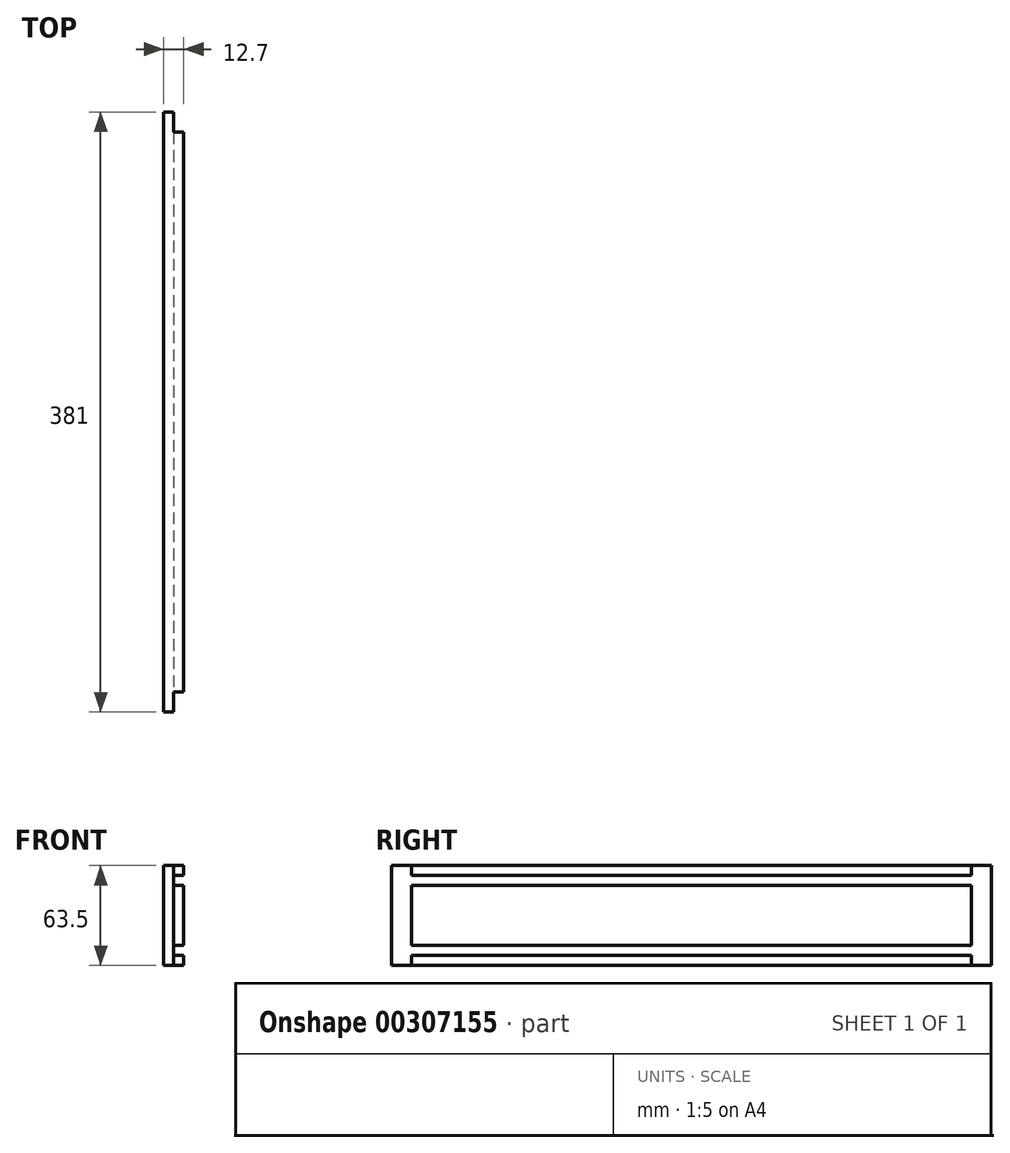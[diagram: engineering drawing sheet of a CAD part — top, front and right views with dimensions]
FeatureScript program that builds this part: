
annotation { "Feature Type Name" : "Feature", "Feature Type Description" : "" }
export const myFeature = defineFeature(function(context is Context, id is Id, definition is map)
    precondition{}
    {
        {
            var Q0;
            Q0=qCreatedBy(makeId("Right.planeOp"),FACE);
            var sketch = newSketch(context, id + "F0", { "sketchPlane" : qUnion([Q0])});
            skLineSegment(sketch, "E0.bottom", {"start": v(190.5, -31.75) * mm, "end": v(-190.5, -31.75) * mm});
            skLineSegment(sketch, "E0.top", {"start": v(190.5, 31.75) * mm, "end": v(-190.5, 31.75) * mm});
            skLineSegment(sketch, "E0.left", {"start": v(190.5, -31.75) * mm, "end": v(190.5, 31.75) * mm});
            skLineSegment(sketch, "E0.right", {"start": v(-190.5, -31.75) * mm, "end": v(-190.5, 31.75) * mm});
            skPoint(sketch, "E0.middle", {"position": v(0, 0) * mm});
            skSolve(sketch);
        }
        {
            var Q0;
            Q0=makeQuery(id+"F0.imprint","IMPRINT",FACE,{"disambiguationData":[TD([[makeQuery(id+"F0.imprint","IMPRINT",EDGE,{"derivedFrom":sQuery(id+"F0.wireOp",EDGE,"E0.bottom")}),-1.0]])]});
            extrude(context, id + "F1", {"entities" : qUnion([Q0]), "depth" : 12.7 * mm});
        }
        {
            var Q0;
            Q0=makeQuery(id+"F1.opExtrude","SWEPT_FACE",FACE,{"disambiguationData":[OSD([sQuery(id+"F0.wireOp",EDGE,"E0.top")])]});
            var sketch = newSketch(context, id + "F2", { "sketchPlane" : qUnion([Q0])});
            skLineSegment(sketch, "E1.bottom", {"start": v(12.7, -190.5) * mm, "end": v(6.35, -190.5) * mm});
            skLineSegment(sketch, "E1.top", {"start": v(12.7, -177.8) * mm, "end": v(6.35, -177.8) * mm});
            skLineSegment(sketch, "E1.left", {"start": v(12.7, -190.5) * mm, "end": v(12.7, -177.8) * mm});
            skLineSegment(sketch, "E1.right", {"start": v(6.35, -190.5) * mm, "end": v(6.35, -177.8) * mm});
            skLineSegment(sketch, "E2.bottom", {"start": v(12.7, 190.5) * mm, "end": v(6.35, 190.5) * mm});
            skLineSegment(sketch, "E2.top", {"start": v(12.7, 177.8) * mm, "end": v(6.35, 177.8) * mm});
            skLineSegment(sketch, "E2.left", {"start": v(12.7, 190.5) * mm, "end": v(12.7, 177.8) * mm});
            skLineSegment(sketch, "E2.right", {"start": v(6.35, 190.5) * mm, "end": v(6.35, 177.8) * mm});
            skSolve(sketch);
        }
        {
            var Q0;
            Q0=makeQuery(id+"F2.imprint","IMPRINT",FACE,{"disambiguationData":[TD([[makeQuery(id+"F2.imprint","IMPRINT",EDGE,{"derivedFrom":sQuery(id+"F2.wireOp",EDGE,"E2.bottom")}),1.0]])]});
            var Q1;
            Q1=makeQuery(id+"F2.imprint","IMPRINT",FACE,{"disambiguationData":[TD([[makeQuery(id+"F2.imprint","IMPRINT",EDGE,{"derivedFrom":sQuery(id+"F2.wireOp",EDGE,"E1.bottom")}),-1.0]])]});
            extrude(context, id + "F3", {"entities" : qUnion([Q0, Q1]), "operationType" : NewBodyOperationType.REMOVE, "endBound" : BoundingType.THROUGH_ALL, "oppositeDirection" : true, "depth" : 25.4 * mm});
        }
        {
            var Q0;
            Q0=makeQuery(id+"F1.opExtrude","CAP_FACE",FACE,{"disambiguationData":[OSD([sQuery(id+"F0.wireOp",EDGE,"E0.bottom"),sQuery(id+"F0.wireOp",EDGE,"E0.top"),sQuery(id+"F0.wireOp",EDGE,"E0.left"),sQuery(id+"F0.wireOp",EDGE,"E0.right")])],"isStart":false});
            var sketch = newSketch(context, id + "F4", { "sketchPlane" : qUnion([Q0])});
            skLineSegment(sketch, "E3.bottom", {"start": v(177.8, 25.4) * mm, "end": v(-177.8, 25.4) * mm});
            skLineSegment(sketch, "E3.top", {"start": v(177.8, 19.05) * mm, "end": v(-177.8, 19.05) * mm});
            skLineSegment(sketch, "E3.left", {"start": v(177.8, 25.4) * mm, "end": v(177.8, 19.05) * mm});
            skLineSegment(sketch, "E3.right", {"start": v(-177.8, 25.4) * mm, "end": v(-177.8, 19.05) * mm});
            skLineSegment(sketch, "E4.bottom", {"start": v(177.8, -19.05) * mm, "end": v(-177.8, -19.05) * mm});
            skLineSegment(sketch, "E4.top", {"start": v(177.8, -25.4) * mm, "end": v(-177.8, -25.4) * mm});
            skLineSegment(sketch, "E4.left", {"start": v(177.8, -19.05) * mm, "end": v(177.8, -25.4) * mm});
            skLineSegment(sketch, "E4.right", {"start": v(-177.8, -19.05) * mm, "end": v(-177.8, -25.4) * mm});
            skSolve(sketch);
        }
        {
            var Q0;
            Q0=makeQuery(id+"F4.imprint","IMPRINT",FACE,{"disambiguationData":[TD([[makeQuery(id+"F4.imprint","IMPRINT",EDGE,{"derivedFrom":sQuery(id+"F4.wireOp",EDGE,"E3.bottom")}),1.0]])]});
            var Q1;
            Q1=makeQuery(id+"F4.imprint","IMPRINT",FACE,{"disambiguationData":[TD([[makeQuery(id+"F4.imprint","IMPRINT",EDGE,{"derivedFrom":sQuery(id+"F4.wireOp",EDGE,"E4.bottom")}),1.0]])]});
            extrude(context, id + "F5", {"entities" : qUnion([Q0, Q1]), "operationType" : NewBodyOperationType.REMOVE, "oppositeDirection" : true, "depth" : 6.35 * mm});
        }
    });
